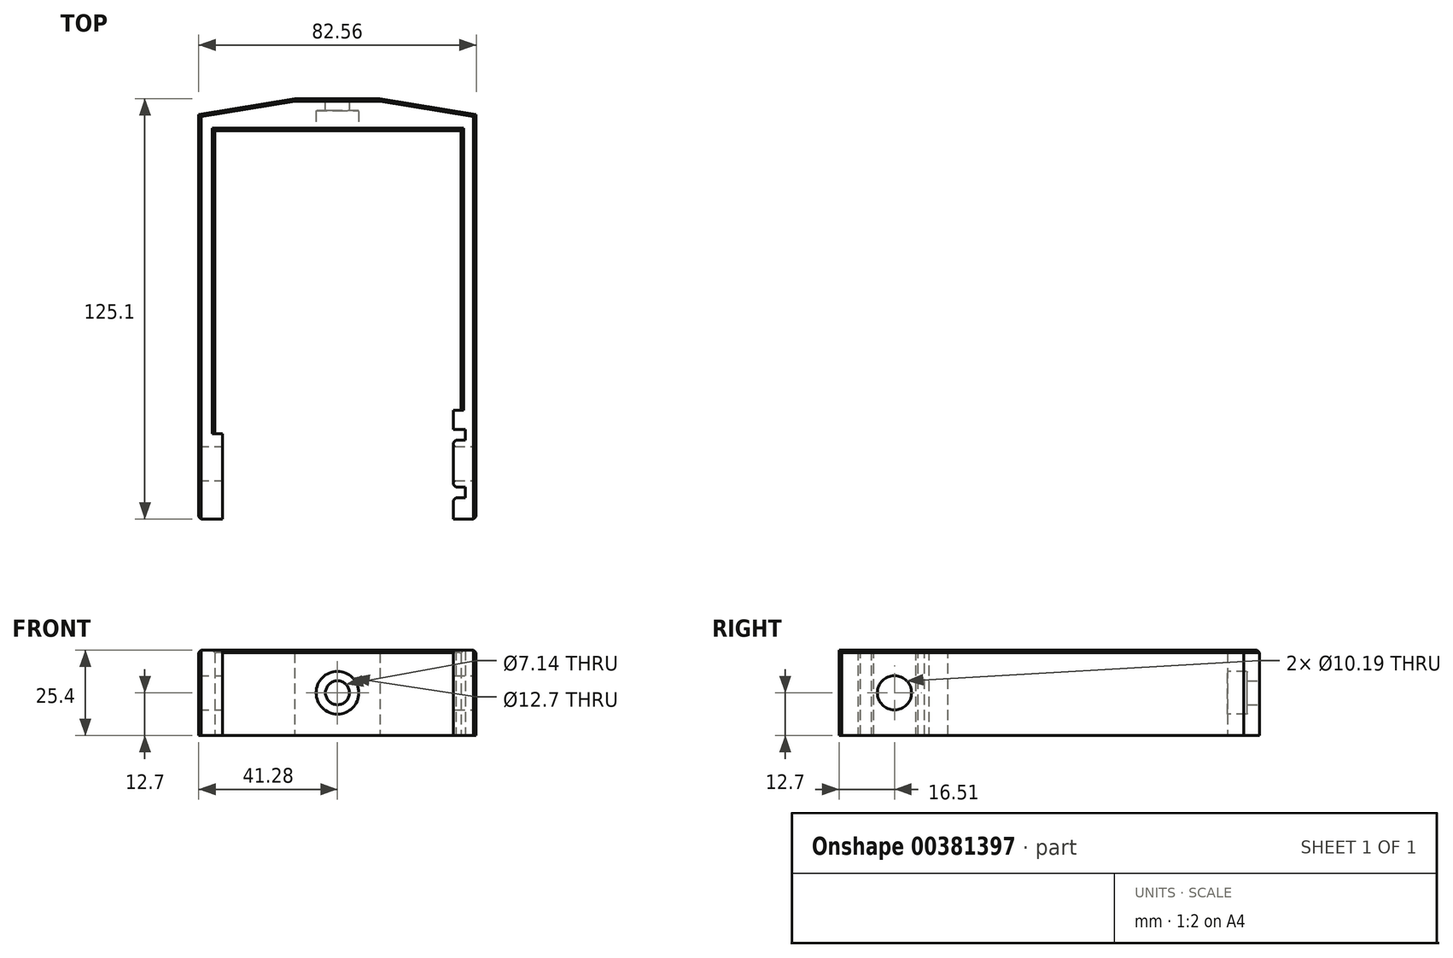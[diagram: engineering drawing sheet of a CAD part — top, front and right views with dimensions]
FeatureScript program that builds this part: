
annotation { "Feature Type Name" : "Feature", "Feature Type Description" : "" }
export const myFeature = defineFeature(function(context is Context, id is Id, definition is map)
    precondition{}
    {
        {
            var Q0;
            Q0=qCreatedBy(makeId("Top.planeOp"),FACE);
            var sketch = newSketch(context, id + "F0", { "sketchPlane" : qUnion([Q0])});
            skLineSegment(sketch, "E0", {"start": v(-41.27, 0) * mm, "end": v(-41.28, 120.4) * mm});
            skLineSegment(sketch, "E1", {"start": v(-12.7, 125.1) * mm, "end": v(0, 125.1) * mm});
            skLineSegment(sketch, "E2", {"start": v(0, 65.12) * mm, "end": v(0, -44.38) * mm, "construction": true});
            skLineSegment(sketch, "E3.MirrorCS", {"start": v(12.7, 125.1) * mm, "end": v(0, 125.1) * mm});
            skLineSegment(sketch, "E4.MirrorCS", {"start": v(41.28, 0) * mm, "end": v(41.28, 120.4) * mm});
            skLineSegment(sketch, "E5.0", {"start": v(36.83, 0) * mm, "end": v(36.83, 115.57) * mm});
            skLineSegment(sketch, "E5.1", {"start": v(36.83, 115.57) * mm, "end": v(0, 115.57) * mm});
            skLineSegment(sketch, "E5.2", {"start": v(-36.45, 115.57) * mm, "end": v(0, 115.57) * mm});
            skLineSegment(sketch, "E5.3", {"start": v(-36.45, 0) * mm, "end": v(-36.45, 115.57) * mm});
            skLineSegment(sketch, "E6", {"start": v(-41.27, 0) * mm, "end": v(-36.45, 0) * mm});
            skLineSegment(sketch, "E7", {"start": v(36.83, 0) * mm, "end": v(41.28, 0) * mm});
            skLineSegment(sketch, "E8", {"start": v(-12.7, 125.1) * mm, "end": v(-41.28, 120.4) * mm});
            skLineSegment(sketch, "E9.MirrorCS", {"start": v(12.7, 125.1) * mm, "end": v(41.28, 120.4) * mm});
            skPoint(sketch, "E10.orphan", {"position": v(-41.28, 125.1) * mm});
            skPoint(sketch, "E11.orphan", {"position": v(41.28, 125.1) * mm});
            skSolve(sketch);
        }
        {
            var Q0;
            Q0 = qSketchRegion(id + "F0", true);
            extrude(context, id + "F1", {"entities" : qUnion([Q0]), "depth" : 25.4 * mm});
        }
        {
            var Q0;
            Q0=qCreatedBy(makeId("Right.planeOp"),FACE);
            var sketch = newSketch(context, id + "F2", { "sketchPlane" : qUnion([Q0])});
            skCircle(sketch, "E12", {"center": v(16.5, 12.7) * mm, "radius": 5.1 * mm});
            skSolve(sketch);
        }
        {
            var Q0;
            Q0=makeQuery(id+"F1.opExtrude","SWEPT_FACE",FACE,{"disambiguationData":[OSD([sQuery(id+"F0.wireOp",EDGE,"E1"),sQuery(id+"F0.wireOp",EDGE,"E3.MirrorCS")])]});
            var sketch = newSketch(context, id + "F3", { "sketchPlane" : qUnion([Q0])});
            skCircle(sketch, "E13", {"center": v(0, 12.7) * mm, "radius": 3.57 * mm});
            skSolve(sketch);
        }
        {
            var Q0;
            Q0=makeQuery(id+"F3.imprint","IMPRINT",FACE,{"disambiguationData":[TD([[makeQuery(id+"F3.imprint","IMPRINT",EDGE,{"derivedFrom":sQuery(id+"F3.wireOp",EDGE,"E13")}),1.0]])]});
            extrude(context, id + "F4", {"entities" : qUnion([Q0]), "operationType" : NewBodyOperationType.REMOVE, "endBound" : BoundingType.UP_TO_NEXT, "oppositeDirection" : true, "depth" : 25.4 * mm});
        }
        {
            var Q0;
            Q0=makeQuery(id+"F1.opExtrude","SWEPT_FACE",FACE,{"disambiguationData":[OSD([sQuery(id+"F0.wireOp",EDGE,"E5.1"),sQuery(id+"F0.wireOp",EDGE,"E5.2")])]});
            var sketch = newSketch(context, id + "F5", { "sketchPlane" : qUnion([Q0])});
            skCircle(sketch, "E14", {"center": v(0, 12.7) * mm, "radius": 6.35 * mm});
            skSolve(sketch);
        }
        {
            var Q0;
            Q0 = qSketchRegion(id + "F5", true);
            extrude(context, id + "F6", {"entities" : qUnion([Q0]), "operationType" : NewBodyOperationType.REMOVE, "oppositeDirection" : true, "depth" : 5.95 * mm});
        }
        {
            var Q0;
            Q0=makeQuery(id+"F1.opExtrude","SWEPT_FACE",FACE,{"disambiguationData":[OSD([sQuery(id+"F0.wireOp",EDGE,"E5.3")])]});
            var sketch = newSketch(context, id + "F7", { "sketchPlane" : qUnion([Q0])});
            skLineSegment(sketch, "E15.bottom", {"start": v(25.4, 0) * mm, "end": v(0, 0) * mm});
            skLineSegment(sketch, "E15.top", {"start": v(0, 25.4) * mm, "end": v(25.4, 25.4) * mm});
            skLineSegment(sketch, "E15.left", {"start": v(0, 0) * mm, "end": v(0, 25.4) * mm});
            skLineSegment(sketch, "E15.right", {"start": v(25.4, 0) * mm, "end": v(25.4, 25.4) * mm});
            skSolve(sketch);
        }
        {
            var Q0;
            Q0 = qSketchRegion(id + "F7", true);
            extrude(context, id + "F8", {"entities" : qUnion([Q0]), "operationType" : NewBodyOperationType.ADD, "depth" : 2.3 * mm, "offsetDistance" : 25.4 * mm});
        }
        {
            var Q0;
            Q0=makeQuery(id+"F2.imprint","IMPRINT",FACE,{"disambiguationData":[TD([[makeQuery(id+"F2.imprint","IMPRINT",EDGE,{"derivedFrom":sQuery(id+"F2.wireOp",EDGE,"E12")}),1.0]])]});
            extrude(context, id + "F9", {"entities" : qUnion([Q0]), "operationType" : NewBodyOperationType.REMOVE, "endBound" : BoundingType.THROUGH_ALL, "oppositeDirection" : true, "depth" : 25.4 * mm, "hasSecondDirection" : true, "secondDirectionBound" : SecondDirectionBoundingType.THROUGH_ALL, "secondDirectionOppositeDirection" : false, "secondDirectionDepth" : 25.4 * mm, "offsetDistance" : 25.4 * mm});
        }
        {
            var Q0;
            Q0=makeQuery(id+"F1.opExtrude","SWEPT_FACE",FACE,{"disambiguationData":[OSD([sQuery(id+"F0.wireOp",EDGE,"E5.0")])]});
            var sketch = newSketch(context, id + "F10", { "sketchPlane" : qUnion([Q0])});
            skLineSegment(sketch, "E16.bottom", {"start": v(0, 0) * mm, "end": v(-32.39, 0) * mm});
            skLineSegment(sketch, "E16.top", {"start": v(0, 25.4) * mm, "end": v(-32.39, 25.4) * mm});
            skLineSegment(sketch, "E16.left", {"start": v(0, 0) * mm, "end": v(0, 25.4) * mm});
            skLineSegment(sketch, "E16.right", {"start": v(-32.39, 0) * mm, "end": v(-32.39, 25.4) * mm});
            skPoint(sketch, "E17", {"position": v(-16.51, 12.7) * mm});
            skSolve(sketch);
        }
        {
            var Q0;
            Q0=makeQuery(id+"F10.imprint","IMPRINT",FACE,{"disambiguationData":[TD([[makeQuery(id+"F10.imprint","IMPRINT",EDGE,{"derivedFrom":sQuery(id+"F10.wireOp",EDGE,"E16.bottom")}),-1.0]])]});
            extrude(context, id + "F11", {"entities" : qUnion([Q0]), "operationType" : NewBodyOperationType.ADD, "depth" : 2.3 * mm, "offsetDistance" : 25.4 * mm});
        }
        {
            var Q0;
            Q0=makeQuery(id+"F1.opExtrude","CAP_EDGE",EDGE,{"disambiguationData":[OSD([sQuery(id+"F0.wireOp",EDGE,"E0")])],"isStart":false});
            var Q1;
            Q1=makeQuery(id+"F1.opExtrude","CAP_EDGE",EDGE,{"disambiguationData":[OSD([sQuery(id+"F0.wireOp",EDGE,"E8")])],"isStart":false});
            var Q2;
            Q2=makeQuery(id+"F1.opExtrude","CAP_EDGE",EDGE,{"disambiguationData":[OSD([sQuery(id+"F0.wireOp",EDGE,"E1"),sQuery(id+"F0.wireOp",EDGE,"E3.MirrorCS")])],"isStart":false});
            var Q3;
            Q3=makeQuery(id+"F1.opExtrude","CAP_EDGE",EDGE,{"disambiguationData":[OSD([sQuery(id+"F0.wireOp",EDGE,"E9.MirrorCS")])],"isStart":false});
            var Q4;
            Q4=makeQuery(id+"F1.opExtrude","CAP_EDGE",EDGE,{"disambiguationData":[OSD([sQuery(id+"F0.wireOp",EDGE,"E4.MirrorCS")])],"isStart":false});
            var Q5;
            Q5=makeQuery(id+"FvB8DFzWzP6xkj0_1.opExtrude","CAP_EDGE",EDGE,{"disambiguationData":[OSD([sQuery(id+"FdAErZO2IQfkYKE_1.wireOp",EDGE,"nKC7WvFg-pDxp-eBRs-fOVh-vdAcKMIAaras.top")])],"isStart":false});
            var Q6;
            Q6=makeQuery(id+"FvB8DFzWzP6xkj0_1.opExtrude","CAP_EDGE",EDGE,{"disambiguationData":[OSD([sQuery(id+"FdAErZO2IQfkYKE_1.wireOp",EDGE,"nKC7WvFg-pDxp-eBRs-fOVh-vdAcKMIAaras.bottom")])],"isStart":false});
            var Q7;
            {var subQ0=sQuery(id+"FdAErZO2IQfkYKE_1.wireOp",EDGE,"nKC7WvFg-pDxp-eBRs-fOVh-vdAcKMIAaras.left");var subQ1=sQuery(id+"FdAErZO2IQfkYKE_1.wireOp",EDGE,"nKC7WvFg-pDxp-eBRs-fOVh-vdAcKMIAaras.bottom");Q7=makeQuery(id+"Ff6aTwWRQvVDFT8_1.opChamfer","BLEND_EDGE",EDGE,{"blendedFrom":[makeQuery(id+"FvB8DFzWzP6xkj0_1.opExtrude","SWEPT_EDGE",EDGE,{"disambiguationData":[OSD([sQuery(id+"F0.wireOp",EDGE,"E5.0"),subQ1,subQ0])]}),makeQuery(id+"FvB8DFzWzP6xkj0_1.opExtrude","CAP_FACE",FACE,{"disambiguationData":[OSD([subQ1,sQuery(id+"FdAErZO2IQfkYKE_1.wireOp",EDGE,"nKC7WvFg-pDxp-eBRs-fOVh-vdAcKMIAaras.top"),subQ0,sQuery(id+"FdAErZO2IQfkYKE_1.wireOp",EDGE,"nKC7WvFg-pDxp-eBRs-fOVh-vdAcKMIAaras.right")])],"isStart":false})],"blendedInto":[makeQuery(id+"FvB8DFzWzP6xkj0_1.opExtrude","CAP_FACE",FACE,{"disambiguationData":[OSD([subQ1,sQuery(id+"FdAErZO2IQfkYKE_1.wireOp",EDGE,"nKC7WvFg-pDxp-eBRs-fOVh-vdAcKMIAaras.top"),subQ0,sQuery(id+"FdAErZO2IQfkYKE_1.wireOp",EDGE,"nKC7WvFg-pDxp-eBRs-fOVh-vdAcKMIAaras.right")])],"isStart":false})]});}
            var Q8;
            {var subQ0=sQuery(id+"FdAErZO2IQfkYKE_1.wireOp",EDGE,"nKC7WvFg-pDxp-eBRs-fOVh-vdAcKMIAaras.left");var subQ1=sQuery(id+"FdAErZO2IQfkYKE_1.wireOp",EDGE,"nKC7WvFg-pDxp-eBRs-fOVh-vdAcKMIAaras.top");Q8=makeQuery(id+"Ff6aTwWRQvVDFT8_1.opChamfer","BLEND_EDGE",EDGE,{"blendedFrom":[makeQuery(id+"FvB8DFzWzP6xkj0_1.opExtrude","SWEPT_EDGE",EDGE,{"disambiguationData":[OSD([sQuery(id+"F0.wireOp",EDGE,"E5.0"),subQ1,subQ0])]}),makeQuery(id+"FvB8DFzWzP6xkj0_1.opExtrude","CAP_FACE",FACE,{"disambiguationData":[OSD([sQuery(id+"FdAErZO2IQfkYKE_1.wireOp",EDGE,"nKC7WvFg-pDxp-eBRs-fOVh-vdAcKMIAaras.bottom"),subQ1,subQ0,sQuery(id+"FdAErZO2IQfkYKE_1.wireOp",EDGE,"nKC7WvFg-pDxp-eBRs-fOVh-vdAcKMIAaras.right")])],"isStart":false})],"blendedInto":[makeQuery(id+"FvB8DFzWzP6xkj0_1.opExtrude","CAP_FACE",FACE,{"disambiguationData":[OSD([sQuery(id+"FdAErZO2IQfkYKE_1.wireOp",EDGE,"nKC7WvFg-pDxp-eBRs-fOVh-vdAcKMIAaras.bottom"),subQ1,subQ0,sQuery(id+"FdAErZO2IQfkYKE_1.wireOp",EDGE,"nKC7WvFg-pDxp-eBRs-fOVh-vdAcKMIAaras.right")])],"isStart":false})]});}
            var Q9;
            {var subQ0=sQuery(id+"FdAErZO2IQfkYKE_1.wireOp",EDGE,"nKC7WvFg-pDxp-eBRs-fOVh-vdAcKMIAaras.right");var subQ1=sQuery(id+"FdAErZO2IQfkYKE_1.wireOp",EDGE,"nKC7WvFg-pDxp-eBRs-fOVh-vdAcKMIAaras.top");Q9=makeQuery(id+"Ff6aTwWRQvVDFT8_1.opChamfer","BLEND_EDGE",EDGE,{"blendedFrom":[makeQuery(id+"FvB8DFzWzP6xkj0_1.opExtrude","SWEPT_EDGE",EDGE,{"disambiguationData":[OSD([sQuery(id+"F0.wireOp",EDGE,"E5.3"),subQ1,subQ0])]}),makeQuery(id+"FvB8DFzWzP6xkj0_1.opExtrude","CAP_FACE",FACE,{"disambiguationData":[OSD([sQuery(id+"FdAErZO2IQfkYKE_1.wireOp",EDGE,"nKC7WvFg-pDxp-eBRs-fOVh-vdAcKMIAaras.bottom"),subQ1,sQuery(id+"FdAErZO2IQfkYKE_1.wireOp",EDGE,"nKC7WvFg-pDxp-eBRs-fOVh-vdAcKMIAaras.left"),subQ0])],"isStart":false})],"blendedInto":[makeQuery(id+"FvB8DFzWzP6xkj0_1.opExtrude","CAP_FACE",FACE,{"disambiguationData":[OSD([sQuery(id+"FdAErZO2IQfkYKE_1.wireOp",EDGE,"nKC7WvFg-pDxp-eBRs-fOVh-vdAcKMIAaras.bottom"),subQ1,sQuery(id+"FdAErZO2IQfkYKE_1.wireOp",EDGE,"nKC7WvFg-pDxp-eBRs-fOVh-vdAcKMIAaras.left"),subQ0])],"isStart":false})]});}
            var Q10;
            {var subQ0=sQuery(id+"FdAErZO2IQfkYKE_1.wireOp",EDGE,"nKC7WvFg-pDxp-eBRs-fOVh-vdAcKMIAaras.right");var subQ1=sQuery(id+"FdAErZO2IQfkYKE_1.wireOp",EDGE,"nKC7WvFg-pDxp-eBRs-fOVh-vdAcKMIAaras.bottom");Q10=makeQuery(id+"Ff6aTwWRQvVDFT8_1.opChamfer","BLEND_EDGE",EDGE,{"blendedFrom":[makeQuery(id+"FvB8DFzWzP6xkj0_1.opExtrude","SWEPT_EDGE",EDGE,{"disambiguationData":[OSD([sQuery(id+"F0.wireOp",EDGE,"E5.3"),subQ1,subQ0])]}),makeQuery(id+"FvB8DFzWzP6xkj0_1.opExtrude","CAP_FACE",FACE,{"disambiguationData":[OSD([subQ1,sQuery(id+"FdAErZO2IQfkYKE_1.wireOp",EDGE,"nKC7WvFg-pDxp-eBRs-fOVh-vdAcKMIAaras.top"),sQuery(id+"FdAErZO2IQfkYKE_1.wireOp",EDGE,"nKC7WvFg-pDxp-eBRs-fOVh-vdAcKMIAaras.left"),subQ0])],"isStart":false})],"blendedInto":[makeQuery(id+"FvB8DFzWzP6xkj0_1.opExtrude","CAP_FACE",FACE,{"disambiguationData":[OSD([subQ1,sQuery(id+"FdAErZO2IQfkYKE_1.wireOp",EDGE,"nKC7WvFg-pDxp-eBRs-fOVh-vdAcKMIAaras.top"),sQuery(id+"FdAErZO2IQfkYKE_1.wireOp",EDGE,"nKC7WvFg-pDxp-eBRs-fOVh-vdAcKMIAaras.left"),subQ0])],"isStart":false})]});}
            var Q11;
            Q11=makeQuery(id+"F1.opExtrude","CAP_EDGE",EDGE,{"disambiguationData":[OSD([sQuery(id+"F0.wireOp",EDGE,"E5.3")])],"isStart":false});
            var Q12;
            Q12=makeQuery(id+"F1.opExtrude","CAP_EDGE",EDGE,{"disambiguationData":[OSD([sQuery(id+"F0.wireOp",EDGE,"E5.1"),sQuery(id+"F0.wireOp",EDGE,"E5.2")])],"isStart":false});
            var Q13;
            {var subQ2=sQuery(id+"F0.wireOp",EDGE,"E5.0");Q13=makeQuery(id+"F11.boolean.opBoolean","SPLIT",EDGE,{"disambiguationData":[TD([makeQuery(id+"F11.opExtrude","SWEPT_FACE",FACE,{"disambiguationData":[OSD([sQuery(id+"F10.wireOp",EDGE,"E16.right")])]})])],"derivedFrom":makeQuery(id+"F1.opExtrude","CAP_EDGE",EDGE,{"disambiguationData":[OSD([subQ2])],"isStart":false})});}
            var Q14;
            Q14=makeQuery(id+"Ff6aTwWRQvVDFT8_1.opChamfer","BLEND_EDGE",EDGE,{"blendedFrom":[makeQuery(id+"F1.opExtrude","CAP_EDGE",EDGE,{"disambiguationData":[OSD([sQuery(id+"F0.wireOp",EDGE,"E6")])],"isStart":false}),makeQuery(id+"F1.opExtrude","SWEPT_FACE",FACE,{"disambiguationData":[OSD([sQuery(id+"F0.wireOp",EDGE,"E0")])]})],"blendedInto":[makeQuery(id+"F1.opExtrude","SWEPT_FACE",FACE,{"disambiguationData":[OSD([sQuery(id+"F0.wireOp",EDGE,"E0")])]})]});
            var Q15;
            Q15=makeQuery(id+"Ff6aTwWRQvVDFT8_1.opChamfer","BLEND_EDGE",EDGE,{"blendedFrom":[makeQuery(id+"F1.opExtrude","CAP_EDGE",EDGE,{"disambiguationData":[OSD([sQuery(id+"F0.wireOp",EDGE,"E6")])],"isStart":false}),makeQuery(id+"F1.opExtrude","SWEPT_FACE",FACE,{"disambiguationData":[OSD([sQuery(id+"F0.wireOp",EDGE,"E5.3")])]})],"blendedInto":[makeQuery(id+"F1.opExtrude","SWEPT_FACE",FACE,{"disambiguationData":[OSD([sQuery(id+"F0.wireOp",EDGE,"E5.3")])]})]});
            var Q16;
            Q16=makeQuery(id+"F1.opExtrude","SWEPT_EDGE",EDGE,{"disambiguationData":[OSD([sQuery(id+"F0.wireOp",EDGE,"E0"),sQuery(id+"F0.wireOp",EDGE,"E6")])]});
            var Q17;
            Q17=makeQuery(id+"F1.opExtrude","SWEPT_EDGE",EDGE,{"disambiguationData":[OSD([sQuery(id+"F0.wireOp",EDGE,"E5.3"),sQuery(id+"F0.wireOp",EDGE,"E6")])]});
            var Q18;
            Q18=makeQuery(id+"Ff6aTwWRQvVDFT8_1.opChamfer","BLEND_EDGE",EDGE,{"blendedFrom":[makeQuery(id+"F1.opExtrude","CAP_EDGE",EDGE,{"disambiguationData":[OSD([sQuery(id+"F0.wireOp",EDGE,"E7")])],"isStart":false}),makeQuery(id+"F1.opExtrude","SWEPT_FACE",FACE,{"disambiguationData":[OSD([sQuery(id+"F0.wireOp",EDGE,"E4.MirrorCS")])]})],"blendedInto":[makeQuery(id+"F1.opExtrude","SWEPT_FACE",FACE,{"disambiguationData":[OSD([sQuery(id+"F0.wireOp",EDGE,"E4.MirrorCS")])]})]});
            var Q19;
            Q19=makeQuery(id+"F1.opExtrude","SWEPT_EDGE",EDGE,{"disambiguationData":[OSD([sQuery(id+"F0.wireOp",EDGE,"E4.MirrorCS"),sQuery(id+"F0.wireOp",EDGE,"E7")])]});
            chamfer(context, id + "F12", {"entities" : qUnion([Q0, Q1, Q2, Q3, Q4, Q5, Q6, Q7, Q8, Q9, Q10, Q11, Q12, Q13, Q14, Q15, Q16, Q17, Q18, Q19]), "width" : 0.76 * mm, "tangentPropagation" : true});
        }
        {
            var Q0;
            Q0=makeQuery(id+"F11.opExtrude","CAP_FACE",FACE,{"disambiguationData":[OSD([sQuery(id+"F0.wireOp",EDGE,"E5.0"),sQuery(id+"F2.wireOp",EDGE,"E12"),sQuery(id+"F10.wireOp",EDGE,"E16.bottom"),sQuery(id+"F10.wireOp",EDGE,"E16.top"),sQuery(id+"F10.wireOp",EDGE,"E16.left"),sQuery(id+"F10.wireOp",EDGE,"E16.right")])],"isStart":false});
            var sketch = newSketch(context, id + "F13", { "sketchPlane" : qUnion([Q0])});
            skLineSegment(sketch, "E18.bottom", {"start": v(-26.67, 25.4) * mm, "end": v(-23.5, 25.4) * mm});
            skLineSegment(sketch, "E18.top", {"start": v(-26.67, 0) * mm, "end": v(-23.5, 0) * mm});
            skLineSegment(sketch, "E18.left", {"start": v(-26.67, 25.4) * mm, "end": v(-26.67, 0) * mm});
            skLineSegment(sketch, "E18.right", {"start": v(-23.5, 25.4) * mm, "end": v(-23.5, 0) * mm});
            skLineSegment(sketch, "E19.bottom", {"start": v(-9.53, 25.4) * mm, "end": v(-6.35, 25.4) * mm});
            skLineSegment(sketch, "E19.top", {"start": v(-9.53, 0) * mm, "end": v(-6.35, 0) * mm});
            skLineSegment(sketch, "E19.left", {"start": v(-9.53, 25.4) * mm, "end": v(-9.53, 0) * mm});
            skLineSegment(sketch, "E19.right", {"start": v(-6.35, 25.4) * mm, "end": v(-6.35, 0) * mm});
            skPoint(sketch, "E20", {"position": v(-16.51, 12.7) * mm});
            skSolve(sketch);
        }
        {
            var Q0;
            Q0 = qSketchRegion(id + "F13", true);
            extrude(context, id + "F14", {"entities" : qUnion([Q0]), "operationType" : NewBodyOperationType.REMOVE, "oppositeDirection" : true, "depth" : 3.56 * mm, "offsetDistance" : 25.4 * mm});
        }
        {
            var Q0;
            Q0=makeQuery(id+"F14.boolean.opBoolean","COPY",EDGE,{"derivedFrom":makeQuery(id+"F14.opExtrude","CAP_EDGE",EDGE,{"disambiguationData":[OSD([sQuery(id+"F13.wireOp",EDGE,"E18.left")])],"isStart":true})});
            var Q1;
            Q1=makeQuery(id+"F14.boolean.opBoolean","COPY",EDGE,{"derivedFrom":makeQuery(id+"F14.opExtrude","CAP_EDGE",EDGE,{"disambiguationData":[OSD([sQuery(id+"F13.wireOp",EDGE,"E18.right")])],"isStart":true})});
            var Q2;
            Q2=makeQuery(id+"F14.boolean.opBoolean","COPY",EDGE,{"derivedFrom":makeQuery(id+"F14.opExtrude","CAP_EDGE",EDGE,{"disambiguationData":[OSD([sQuery(id+"F13.wireOp",EDGE,"E19.left")])],"isStart":true})});
            var Q3;
            Q3=makeQuery(id+"F14.boolean.opBoolean","COPY",EDGE,{"derivedFrom":makeQuery(id+"F14.opExtrude","CAP_EDGE",EDGE,{"disambiguationData":[OSD([sQuery(id+"F13.wireOp",EDGE,"E19.right")])],"isStart":true})});
            var Q4;
            Q4=makeQuery(id+"F11.opExtrude","CAP_EDGE",EDGE,{"disambiguationData":[OSD([sQuery(id+"F10.wireOp",EDGE,"E16.right")])],"isStart":true});
            var Q5;
            Q5=makeQuery(id+"F1OoklNMJk3Q5tj_1.opExtrude","CAP_EDGE",EDGE,{"disambiguationData":[OSD([sQuery(id+"FLh77HAkqBR3Zce_1.wireOp",EDGE,"tzFSXb0X-AYiK-pux7-b0Qk-k0YHHgHK4CI7.right")])],"isStart":true});
            var Q6;
            Q6=makeQuery(id+"F1OoklNMJk3Q5tj_1.opExtrude","CAP_EDGE",EDGE,{"disambiguationData":[OSD([sQuery(id+"FLh77HAkqBR3Zce_1.wireOp",EDGE,"tzFSXb0X-AYiK-pux7-b0Qk-k0YHHgHK4CI7.left")])],"isStart":true});
            var Q7;
            Q7=makeQuery(id+"F1OoklNMJk3Q5tj_1.opExtrude","CAP_EDGE",EDGE,{"disambiguationData":[OSD([sQuery(id+"FLh77HAkqBR3Zce_1.wireOp",EDGE,"aiTMODUb-hr5M-VeDR-0KCh-ahNu4iZaUgDT.left")])],"isStart":true});
            var Q8;
            Q8=makeQuery(id+"F1OoklNMJk3Q5tj_1.opExtrude","CAP_EDGE",EDGE,{"disambiguationData":[OSD([sQuery(id+"FLh77HAkqBR3Zce_1.wireOp",EDGE,"aiTMODUb-hr5M-VeDR-0KCh-ahNu4iZaUgDT.right")])],"isStart":true});
            chamfer(context, id + "F15", {"entities" : qUnion([Q0, Q1, Q2, Q3, Q4, Q5, Q6, Q7, Q8]), "width" : 0.76 * mm, "tangentPropagation" : true});
        }
        {
            var Q0;
            Q0=makeQuery(id+"F6.boolean.opBoolean","COPY",EDGE,{"derivedFrom":makeQuery(id+"F6.opExtrude","CAP_EDGE",EDGE,{"disambiguationData":[OSD([sQuery(id+"F5.wireOp",EDGE,"E14")])],"isStart":false})});
            fillet(context, id + "F16", {"entities" : qUnion([Q0]), "radius" : 0.25 * mm, "tangentPropagation" : true, "allowEdgeOverflow" : false});
        }
        {
            var Q0;
            Q0=makeQuery(id+"FvB8DFzWzP6xkj0_1.opExtrude","SWEPT_EDGE",EDGE,{"disambiguationData":[OSD([sQuery(id+"F0.wireOp",EDGE,"E5.0"),sQuery(id+"FdAErZO2IQfkYKE_1.wireOp",EDGE,"nKC7WvFg-pDxp-eBRs-fOVh-vdAcKMIAaras.bottom"),sQuery(id+"FdAErZO2IQfkYKE_1.wireOp",EDGE,"nKC7WvFg-pDxp-eBRs-fOVh-vdAcKMIAaras.left")])]});
            var Q1;
            Q1=makeQuery(id+"F12.opChamfer","BLEND_EDGE",EDGE,{"blendedFrom":[makeQuery(id+"FvB8DFzWzP6xkj0_1.opExtrude","CAP_EDGE",EDGE,{"disambiguationData":[OSD([sQuery(id+"FdAErZO2IQfkYKE_1.wireOp",EDGE,"nKC7WvFg-pDxp-eBRs-fOVh-vdAcKMIAaras.bottom")])],"isStart":false}),makeQuery(id+"F1.opExtrude","SWEPT_FACE",FACE,{"disambiguationData":[OSD([sQuery(id+"F0.wireOp",EDGE,"E5.0")])]})],"blendedInto":[makeQuery(id+"F1.opExtrude","SWEPT_FACE",FACE,{"disambiguationData":[OSD([sQuery(id+"F0.wireOp",EDGE,"E5.0")])]})]});
            var Q2;
            Q2=makeQuery(id+"FvB8DFzWzP6xkj0_1.opExtrude","CAP_EDGE",EDGE,{"disambiguationData":[OSD([sQuery(id+"FdAErZO2IQfkYKE_1.wireOp",EDGE,"nKC7WvFg-pDxp-eBRs-fOVh-vdAcKMIAaras.left")])],"isStart":false});
            var Q3;
            Q3=makeQuery(id+"F12.opChamfer","BLEND_EDGE",EDGE,{"blendedFrom":[makeQuery(id+"FvB8DFzWzP6xkj0_1.opExtrude","CAP_EDGE",EDGE,{"disambiguationData":[OSD([sQuery(id+"FdAErZO2IQfkYKE_1.wireOp",EDGE,"nKC7WvFg-pDxp-eBRs-fOVh-vdAcKMIAaras.top")])],"isStart":false}),makeQuery(id+"F1.opExtrude","SWEPT_FACE",FACE,{"disambiguationData":[OSD([sQuery(id+"F0.wireOp",EDGE,"E5.0")])]})],"blendedInto":[makeQuery(id+"F1.opExtrude","SWEPT_FACE",FACE,{"disambiguationData":[OSD([sQuery(id+"F0.wireOp",EDGE,"E5.0")])]})]});
            var Q4;
            Q4=makeQuery(id+"FvB8DFzWzP6xkj0_1.opExtrude","SWEPT_EDGE",EDGE,{"disambiguationData":[OSD([sQuery(id+"F0.wireOp",EDGE,"E5.0"),sQuery(id+"FdAErZO2IQfkYKE_1.wireOp",EDGE,"nKC7WvFg-pDxp-eBRs-fOVh-vdAcKMIAaras.top"),sQuery(id+"FdAErZO2IQfkYKE_1.wireOp",EDGE,"nKC7WvFg-pDxp-eBRs-fOVh-vdAcKMIAaras.left")])]});
            var Q5;
            Q5=makeQuery(id+"FvB8DFzWzP6xkj0_1.opExtrude","SWEPT_EDGE",EDGE,{"disambiguationData":[OSD([sQuery(id+"F0.wireOp",EDGE,"E5.3"),sQuery(id+"FdAErZO2IQfkYKE_1.wireOp",EDGE,"nKC7WvFg-pDxp-eBRs-fOVh-vdAcKMIAaras.bottom"),sQuery(id+"FdAErZO2IQfkYKE_1.wireOp",EDGE,"nKC7WvFg-pDxp-eBRs-fOVh-vdAcKMIAaras.right")])]});
            var Q6;
            Q6=makeQuery(id+"F12.opChamfer","BLEND_EDGE",EDGE,{"blendedFrom":[makeQuery(id+"FvB8DFzWzP6xkj0_1.opExtrude","CAP_EDGE",EDGE,{"disambiguationData":[OSD([sQuery(id+"FdAErZO2IQfkYKE_1.wireOp",EDGE,"nKC7WvFg-pDxp-eBRs-fOVh-vdAcKMIAaras.bottom")])],"isStart":false}),makeQuery(id+"F1.opExtrude","SWEPT_FACE",FACE,{"disambiguationData":[OSD([sQuery(id+"F0.wireOp",EDGE,"E5.3")])]})],"blendedInto":[makeQuery(id+"F1.opExtrude","SWEPT_FACE",FACE,{"disambiguationData":[OSD([sQuery(id+"F0.wireOp",EDGE,"E5.3")])]})]});
            var Q7;
            Q7=makeQuery(id+"FvB8DFzWzP6xkj0_1.opExtrude","CAP_EDGE",EDGE,{"disambiguationData":[OSD([sQuery(id+"FdAErZO2IQfkYKE_1.wireOp",EDGE,"nKC7WvFg-pDxp-eBRs-fOVh-vdAcKMIAaras.right")])],"isStart":false});
            var Q8;
            Q8=makeQuery(id+"F12.opChamfer","BLEND_EDGE",EDGE,{"blendedFrom":[makeQuery(id+"FvB8DFzWzP6xkj0_1.opExtrude","CAP_EDGE",EDGE,{"disambiguationData":[OSD([sQuery(id+"FdAErZO2IQfkYKE_1.wireOp",EDGE,"nKC7WvFg-pDxp-eBRs-fOVh-vdAcKMIAaras.top")])],"isStart":false}),makeQuery(id+"F1.opExtrude","SWEPT_FACE",FACE,{"disambiguationData":[OSD([sQuery(id+"F0.wireOp",EDGE,"E5.3")])]})],"blendedInto":[makeQuery(id+"F1.opExtrude","SWEPT_FACE",FACE,{"disambiguationData":[OSD([sQuery(id+"F0.wireOp",EDGE,"E5.3")])]})]});
            var Q9;
            Q9=makeQuery(id+"FvB8DFzWzP6xkj0_1.opExtrude","SWEPT_EDGE",EDGE,{"disambiguationData":[OSD([sQuery(id+"F0.wireOp",EDGE,"E5.3"),sQuery(id+"FdAErZO2IQfkYKE_1.wireOp",EDGE,"nKC7WvFg-pDxp-eBRs-fOVh-vdAcKMIAaras.top"),sQuery(id+"FdAErZO2IQfkYKE_1.wireOp",EDGE,"nKC7WvFg-pDxp-eBRs-fOVh-vdAcKMIAaras.right")])]});
            var Q10;
            Q10=makeQuery(id+"F1.opExtrude","SWEPT_EDGE",EDGE,{"disambiguationData":[OSD([sQuery(id+"F0.wireOp",EDGE,"E5.2"),sQuery(id+"F0.wireOp",EDGE,"E5.3")])]});
            var Q11;
            Q11=makeQuery(id+"F1.opExtrude","SWEPT_EDGE",EDGE,{"disambiguationData":[OSD([sQuery(id+"F0.wireOp",EDGE,"E5.0"),sQuery(id+"F0.wireOp",EDGE,"E5.1")])]});
            var Q12;
            Q12=makeQuery(id+"F11.opExtrude","CAP_EDGE",EDGE,{"disambiguationData":[OSD([sQuery(id+"F0.wireOp",EDGE,"E5.0"),sQuery(id+"F2.wireOp",EDGE,"E12")])],"isStart":false});
            var Q13;
            Q13=makeQuery(id+"F9.boolean.opBoolean","INTERSECT",EDGE,{"derivedFrom":[makeQuery(id+"F1.opExtrude","SWEPT_FACE",FACE,{"disambiguationData":[OSD([sQuery(id+"F0.wireOp",EDGE,"E4.MirrorCS")])]}),makeQuery(id+"F9.opExtrude","SWEPT_FACE",FACE,{"disambiguationData":[OSD([sQuery(id+"F2.wireOp",EDGE,"E12")])]})]});
            fillet(context, id + "F17", {"entities" : qUnion([Q0, Q1, Q2, Q3, Q4, Q5, Q6, Q7, Q8, Q9, Q10, Q11, Q12, Q13]), "radius" : 0.38 * mm, "tangentPropagation" : true, "allowEdgeOverflow" : false});
        }
    });
